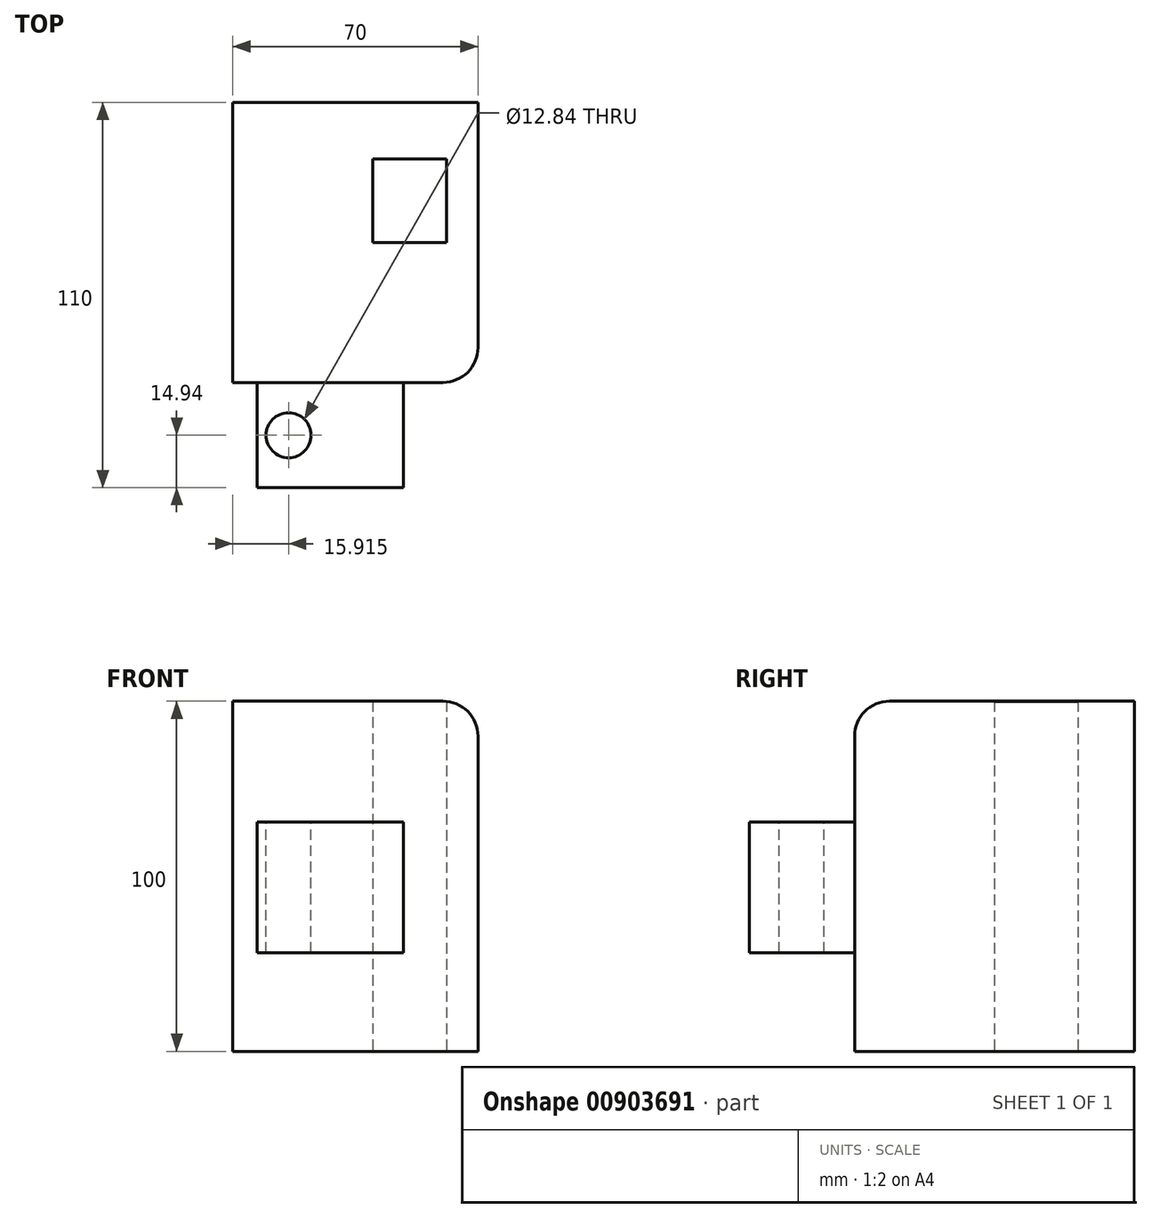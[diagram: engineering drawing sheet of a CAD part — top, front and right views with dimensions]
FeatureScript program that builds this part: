
annotation { "Feature Type Name" : "Feature", "Feature Type Description" : "" }
export const myFeature = defineFeature(function(context is Context, id is Id, definition is map)
    precondition{}
    {
        {
            var Q0;
            Q0=qCreatedBy(makeId("Top.planeOp"),FACE);
            var sketch = newSketch(context, id + "F0", { "sketchPlane" : qUnion([Q0])});
            skLineSegment(sketch, "E0.bottom", {"start": v(-40.8, 41.85) * mm, "end": v(29.2, 41.85) * mm});
            skLineSegment(sketch, "E0.top", {"start": v(-40.8, -38.15) * mm, "end": v(29.2, -38.15) * mm});
            skLineSegment(sketch, "E0.left", {"start": v(-40.8, 41.85) * mm, "end": v(-40.8, -38.15) * mm});
            skLineSegment(sketch, "E0.right", {"start": v(29.2, 41.85) * mm, "end": v(29.2, -38.15) * mm});
            skLineSegment(sketch, "E1.bottom", {"start": v(-0.8, 25.73) * mm, "end": v(20.2, 25.73) * mm});
            skLineSegment(sketch, "E1.top", {"start": v(-0.8, 1.85) * mm, "end": v(20.2, 1.85) * mm});
            skLineSegment(sketch, "E1.left", {"start": v(-0.8, 25.73) * mm, "end": v(-0.8, 1.85) * mm});
            skLineSegment(sketch, "E1.right", {"start": v(20.2, 25.73) * mm, "end": v(20.2, 1.85) * mm});
            skSolve(sketch);
        }
        {
            var Q0;
            Q0=makeQuery(id+"F0.imprint","IMPRINT",FACE,{"disambiguationData":[TD([[makeQuery(id+"F0.imprint","IMPRINT",EDGE,{"derivedFrom":sQuery(id+"F0.wireOp",EDGE,"E0.bottom")}),-1.0]])]});
            extrude(context, id + "F1", {"entities" : qUnion([Q0]), "depth" : 100 * mm, "offsetDistance" : 25 * mm});
        }
        {
            var Q0;
            Q0=makeQuery(id+"F1.opExtrude","SWEPT_FACE",FACE,{"disambiguationData":[OSD([sQuery(id+"F0.wireOp",EDGE,"E0.top")])]});
            var sketch = newSketch(context, id + "F2", { "sketchPlane" : qUnion([Q0])});
            skLineSegment(sketch, "E2.bottom", {"start": v(-33.9, 65.47) * mm, "end": v(7.97, 65.47) * mm});
            skLineSegment(sketch, "E2.top", {"start": v(-33.9, 28.17) * mm, "end": v(7.97, 28.17) * mm});
            skLineSegment(sketch, "E2.left", {"start": v(-33.9, 65.47) * mm, "end": v(-33.9, 28.17) * mm});
            skLineSegment(sketch, "E2.right", {"start": v(7.97, 65.47) * mm, "end": v(7.97, 28.17) * mm});
            skSolve(sketch);
        }
        {
            var Q0;
            Q0=makeQuery(id+"F2.imprint","IMPRINT",FACE,{"disambiguationData":[TD([[makeQuery(id+"F2.imprint","IMPRINT",EDGE,{"derivedFrom":sQuery(id+"F2.wireOp",EDGE,"E2.bottom")}),-1.0]])]});
            extrude(context, id + "F3", {"entities" : qUnion([Q0]), "operationType" : NewBodyOperationType.ADD, "depth" : 30 * mm, "offsetDistance" : 25 * mm});
        }
        {
            var Q0;
            Q0=makeQuery(id+"F3.opExtrude","SWEPT_FACE",FACE,{"disambiguationData":[OSD([sQuery(id+"F2.wireOp",EDGE,"E2.bottom")])]});
            var sketch = newSketch(context, id + "F4", { "sketchPlane" : qUnion([Q0])});
            skCircle(sketch, "E3", {"center": v(-24.88, -53.2) * mm, "radius": 6.42 * mm});
            skSolve(sketch);
        }
        {
            var Q0;
            Q0 = qSketchRegion(id + "F4", true);
            extrude(context, id + "F5", {"entities" : qUnion([Q0]), "operationType" : NewBodyOperationType.REMOVE, "oppositeDirection" : true, "depth" : 50 * mm, "offsetDistance" : 25 * mm});
        }
        {
            var Q0;
            Q0=makeQuery(id+"F1.opExtrude","CAP_EDGE",EDGE,{"disambiguationData":[OSD([sQuery(id+"F0.wireOp",EDGE,"E0.top")])],"isStart":false});
            var Q1;
            Q1=makeQuery(id+"F1.opExtrude","CAP_EDGE",EDGE,{"disambiguationData":[OSD([sQuery(id+"F0.wireOp",EDGE,"E0.right")])],"isStart":false});
            var Q2;
            Q2=makeQuery(id+"F1.opExtrude","SWEPT_EDGE",EDGE,{"disambiguationData":[OSD([sQuery(id+"F0.wireOp",EDGE,"E0.top"),sQuery(id+"F0.wireOp",EDGE,"E0.right")])]});
            fillet(context, id + "F6", {"entities" : qUnion([Q0, Q1, Q2]), "radius" : 10 * mm, "tangentPropagation" : true, "allowEdgeOverflow" : false});
        }
    });
